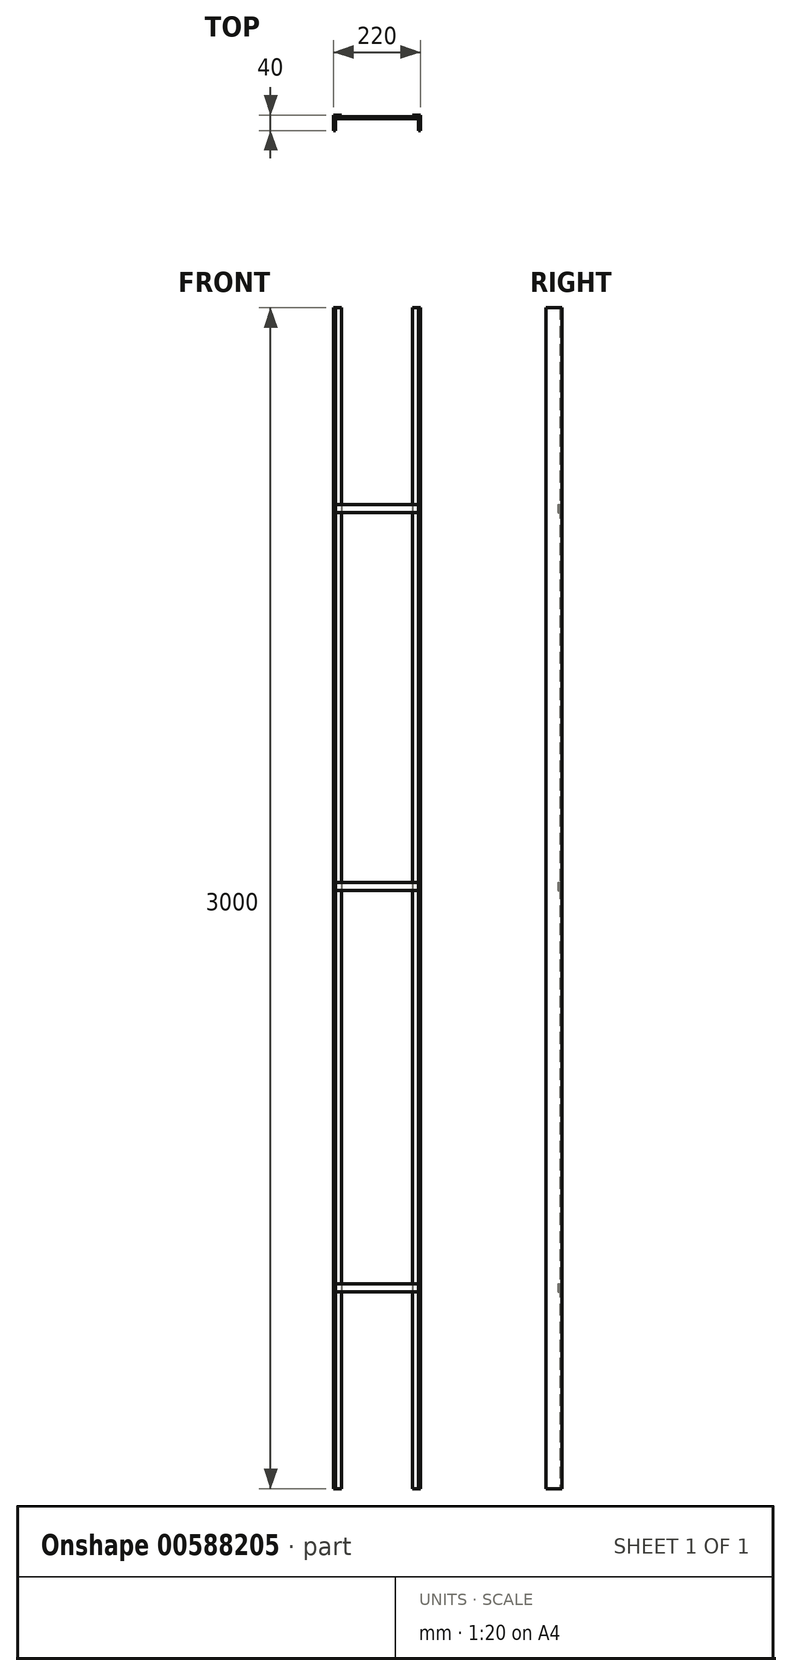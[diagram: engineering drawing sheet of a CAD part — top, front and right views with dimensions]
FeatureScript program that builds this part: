
annotation { "Feature Type Name" : "Feature", "Feature Type Description" : "" }
export const myFeature = defineFeature(function(context is Context, id is Id, definition is map)
    precondition{}
    {
        {
            var Q0;
            Q0=qCreatedBy(makeId("Top.planeOp"),FACE);
            var sketch = newSketch(context, id + "F0", { "sketchPlane" : qUnion([Q0])});
            skLineSegment(sketch, "E0", {"start": v(-55, 55) * mm, "end": v(-35, 55) * mm});
            skLineSegment(sketch, "E1", {"start": v(-35, 55) * mm, "end": v(-35, 50) * mm});
            skLineSegment(sketch, "E2", {"start": v(-35, 50) * mm, "end": v(-50, 50) * mm});
            skLineSegment(sketch, "E3", {"start": v(-50, 50) * mm, "end": v(-50, 15) * mm});
            skLineSegment(sketch, "E4", {"start": v(-50, 15) * mm, "end": v(-55, 15) * mm});
            skLineSegment(sketch, "E5", {"start": v(-55, 15) * mm, "end": v(-55, 55) * mm});
            skLineSegment(sketch, "E6", {"start": v(145, 55) * mm, "end": v(145, 50) * mm});
            skLineSegment(sketch, "E7", {"start": v(145, 50) * mm, "end": v(160, 50) * mm});
            skLineSegment(sketch, "E8", {"start": v(160, 50) * mm, "end": v(160, 15) * mm});
            skLineSegment(sketch, "E9", {"start": v(160, 15) * mm, "end": v(165, 15) * mm});
            skLineSegment(sketch, "E10", {"start": v(165, 15) * mm, "end": v(165, 55) * mm});
            skLineSegment(sketch, "E11", {"start": v(165, 55) * mm, "end": v(145, 55) * mm});
            skSolve(sketch);
        }
        {
            var Q0;
            Q0=makeQuery(id+"F0.imprint","IMPRINT",FACE,{"disambiguationData":[TD([[makeQuery(id+"F0.imprint","IMPRINT",EDGE,{"derivedFrom":sQuery(id+"F0.wireOp",EDGE,"E0")}),-1.0]])]});
            var Q1;
            Q1=makeQuery(id+"F0.imprint","IMPRINT",FACE,{"disambiguationData":[TD([[makeQuery(id+"F0.imprint","IMPRINT",EDGE,{"derivedFrom":sQuery(id+"F0.wireOp",EDGE,"E6")}),1.0]])]});
            extrude(context, id + "F1", {"entities" : qUnion([Q0, Q1]), "depth" : 3000 * mm, "offsetDistance" : 25 * mm});
        }
        {
            var Q0;
            Q0=makeQuery(id+"F1.opExtrude","SWEPT_FACE",FACE,{"disambiguationData":[OSD([sQuery(id+"F0.wireOp",EDGE,"E2")])]});
            var sketch = newSketch(context, id + "F2", { "sketchPlane" : qUnion([Q0])});
            skLineSegment(sketch, "E12.bottom", {"start": v(-50, 2500) * mm, "end": v(160, 2500) * mm});
            skLineSegment(sketch, "E12.top", {"start": v(-50, 2480) * mm, "end": v(160, 2480) * mm});
            skLineSegment(sketch, "E12.left", {"start": v(-50, 2500) * mm, "end": v(-50, 2480) * mm});
            skLineSegment(sketch, "E12.right", {"start": v(160, 2500) * mm, "end": v(160, 2480) * mm});
            skSolve(sketch);
        }
        {
            var Q0;
            Q0 = qSketchRegion(id + "F2", true);
            extrude(context, id + "F3", {"entities" : qUnion([Q0]), "depth" : 5 * mm, "offsetDistance" : 25 * mm});
        }
        {
            var Q0;
            Q0=makeQuery(id+"F1.opExtrude","SWEPT_FACE",FACE,{"disambiguationData":[OSD([sQuery(id+"F0.wireOp",EDGE,"E2")])]});
            var sketch = newSketch(context, id + "F4", { "sketchPlane" : qUnion([Q0])});
            skLineSegment(sketch, "E13.bottom", {"start": v(-50, 500) * mm, "end": v(160, 500) * mm});
            skLineSegment(sketch, "E13.top", {"start": v(-50, 520) * mm, "end": v(160, 520) * mm});
            skLineSegment(sketch, "E13.left", {"start": v(-50, 500) * mm, "end": v(-50, 520) * mm});
            skLineSegment(sketch, "E13.right", {"start": v(160, 500) * mm, "end": v(160, 520) * mm});
            skSolve(sketch);
        }
        {
            var Q0;
            Q0 = qSketchRegion(id + "F4", true);
            extrude(context, id + "F5", {"entities" : qUnion([Q0]), "depth" : 5 * mm, "offsetDistance" : 25 * mm});
        }
        {
            var Q0;
            Q0=makeQuery(id+"F1.opExtrude","SWEPT_FACE",FACE,{"disambiguationData":[OSD([sQuery(id+"F0.wireOp",EDGE,"E2")])]});
            var sketch = newSketch(context, id + "F6", { "sketchPlane" : qUnion([Q0])});
            skLineSegment(sketch, "E14.bottom", {"start": v(-50, 1520) * mm, "end": v(160, 1520) * mm});
            skLineSegment(sketch, "E14.top", {"start": v(-50, 1540) * mm, "end": v(160, 1540) * mm});
            skLineSegment(sketch, "E14.left", {"start": v(-50, 1520) * mm, "end": v(-50, 1540) * mm});
            skLineSegment(sketch, "E14.right", {"start": v(160, 1520) * mm, "end": v(160, 1540) * mm});
            skSolve(sketch);
        }
        {
            var Q0;
            Q0 = qSketchRegion(id + "F6", true);
            extrude(context, id + "F7", {"entities" : qUnion([Q0]), "depth" : 5 * mm, "offsetDistance" : 25 * mm});
        }
    });
